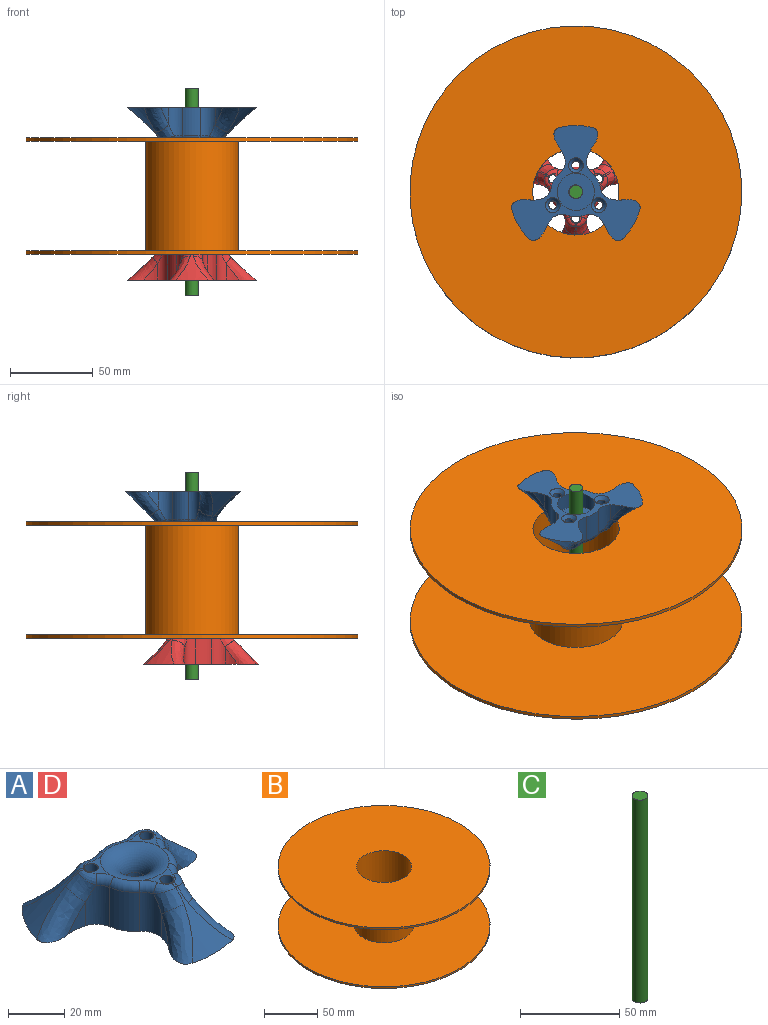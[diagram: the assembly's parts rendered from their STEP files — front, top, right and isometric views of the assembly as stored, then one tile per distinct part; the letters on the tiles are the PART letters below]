
ASSEMBLY  parts=4 mates=3
PART A: 62 faces, bbox 88.5x80.4x33.9 mm
  f0: plane 12.74x8.35mm, normal (0,0,1), area 30.5mm2, adj f13,f44,f46,f48,f50,f52,f61
  f1: plane 11.39x10.93mm, normal (0,0,1), area 30.5mm2, adj f11,f45,f47,f49,f51,f53,f61
  f2: cylinder r=20mm len=10.06mm, axis (0,0,-1), area 41.7mm2, adj f15,f26,f39
  f3: cylinder r=15mm len=17mm, axis (0,0,-1), area 190.3mm2, adj f15,f26,f27,f54
  f4: cylinder r=20mm len=10.06mm, axis (0,0,-1), area 41.7mm2, adj f15,f27,f37
  f5: cylinder r=20mm len=10.06mm, axis (0,0,-1), area 41.7mm2, adj f15,f28,f35
  f6: cylinder r=15mm len=17mm, axis (0,0,-1), area 190.3mm2, adj f15,f28,f29,f55
  f7: cylinder r=20mm len=10.06mm, axis (0,0,-1), area 41.7mm2, adj f15,f29,f33
  f8: cylinder r=20mm len=10.06mm, axis (0,0,-1), area 41.7mm2, adj f15,f30,f31
  f9: cylinder r=15mm len=17mm, axis (0,0,-1), area 190.3mm2, adj f15,f25,f30,f43
  f10: cylinder r=20mm len=10.06mm, axis (0,0,-1), area 41.7mm2, adj f15,f25,f41
  f11: cylinder r=2.5mm len=18mm, axis (0,0,-1), area 282.7mm2, adj f1,f23
  f12: cylinder r=2.5mm len=18mm, axis (0,0,-1), area 282.7mm2, adj f20,f24
  f13: cylinder r=2.5mm len=18mm, axis (0,0,-1), area 282.7mm2, adj f0,f22
  f14: cylinder r=11.2mm len=22.4mm, axis (0,0,-1), area 703.7mm2, adj f15,f21
  f15: plane 82.2x74.09mm, normal (0,0,-1), area 1592.4mm2, adj f2,f3,f4,f5,f6,f7,f8,f9
  f16: cone r=20mm half-angle=45deg, axis (0,0,-1), area 210.3mm2, adj f15,f31,f32,f33,f34,f49
  f17: cone r=20mm half-angle=45deg, axis (0,0,-1), area 210.3mm2, adj f15,f39,f40,f41,f42,f48
  f18: cylinder r=4.2mm len=8.4mm, axis (0,0,-1), area 52.8mm2, adj f21,f61
  f19: cone r=20mm half-angle=45deg, axis (0,0,-1), area 210.3mm2, adj f15,f35,f36,f37,f38,f60
  f20: plane 11.39x10.93mm, normal (0,0,1), area 30.5mm2, adj f12,f56,f57,f58,f59,f60,f61
  f21: plane 22.4x22.4mm, normal (0,0,-1), area 338.7mm2, adj f14,f18
  f22: cone r=4.5mm half-angle=45deg, axis (0,0,-1), area 62.2mm2, adj f13,f15
  f23: cone r=4.5mm half-angle=45deg, axis (0,0,-1), area 62.2mm2, adj f11,f15
  f24: cone r=4.5mm half-angle=45deg, axis (0,0,-1), area 62.2mm2, adj f12,f15
  f25: cylinder r=8mm len=17mm, axis (0,0,-1), area 142.1mm2, adj f9,f10,f15,f42,f44
  f26: cylinder r=8mm len=17mm, axis (0,0,-1), area 142.1mm2, adj f2,f3,f15,f40,f52
  f27: cylinder r=8mm len=17mm, axis (0,0,-1), area 142.1mm2, adj f3,f4,f15,f38,f56
  f28: cylinder r=8mm len=17mm, axis (0,0,-1), area 142.1mm2, adj f5,f6,f15,f36,f57
  f29: cylinder r=8mm len=17mm, axis (0,0,-1), area 142.1mm2, adj f6,f7,f15,f34,f53
  f30: cylinder r=8mm len=17mm, axis (0,0,-1), area 142.1mm2, adj f8,f9,f15,f32,f45
  f31: bspline ~24.84x23.53mm, area 183.7mm2, adj f8,f15,f16,f32
  f32: bspline ~12.71x10.25mm, area 67.7mm2, adj f16,f30,f31,f47
  f33: bspline ~24.84x23.26mm, area 183.7mm2, adj f7,f15,f16,f34
  f34: bspline ~13.09x12.45mm, area 67.7mm2, adj f16,f29,f33,f51
  f35: bspline ~24.84x23.26mm, area 183.7mm2, adj f5,f15,f19,f36
  f36: bspline ~13.09x12.45mm, area 67.7mm2, adj f19,f28,f35,f59
  f37: bspline ~24.84x23.53mm, area 183.7mm2, adj f4,f15,f19,f38
  f38: bspline ~12.71x10.25mm, area 67.7mm2, adj f19,f27,f37,f58
  f39: bspline ~22.82x21.44mm, area 183.7mm2, adj f2,f15,f17,f40
  f40: bspline ~13.09x11.26mm, area 67.7mm2, adj f17,f26,f39,f50
  f41: bspline ~24.84x23.2mm, area 183.7mm2, adj f10,f15,f17,f42
  f42: bspline ~13.09x11.26mm, area 67.7mm2, adj f17,f25,f41,f46
  f43: torus R=12mm, axis (0,0,1), area 48.2mm2, adj f9,f44,f45,f61
  f44: torus R=11mm, axis (0,0,1), area 27.6mm2, adj f0,f25,f43,f46,f61
  f45: torus R=11mm, axis (0,0,1), area 27.6mm2, adj f1,f30,f43,f47,f61
  f46: bspline ~7.24x5.81mm, area 23mm2, adj f0,f42,f44,f48
  f47: bspline ~9.05x4.7mm, area 23mm2, adj f1,f32,f45,f49
  f48: torus R=18.76mm, axis (0,0,1), area 2.4mm2, adj f0,f17,f46,f50
  f49: torus R=18.76mm, axis (0,0,1), area 2.4mm2, adj f1,f16,f47,f51
  f50: bspline ~7.78x6.43mm, area 23mm2, adj f0,f40,f48,f52
  f51: bspline ~7.97x4.64mm, area 23mm2, adj f1,f34,f49,f53
  f52: torus R=11mm, axis (0,0,1), area 27.6mm2, adj f0,f26,f50,f54,f61
  f53: torus R=11mm, axis (0,0,1), area 27.6mm2, adj f1,f29,f51,f55,f61
  f54: torus R=12mm, axis (0,0,1), area 48.2mm2, adj f3,f52,f56,f61
  f55: torus R=12mm, axis (0,0,1), area 48.2mm2, adj f6,f53,f57,f61
  f56: torus R=11mm, axis (0,0,1), area 27.6mm2, adj f20,f27,f54,f58,f61
  f57: torus R=11mm, axis (0,0,1), area 27.6mm2, adj f20,f28,f55,f59,f61
  f58: bspline ~8.78x4.22mm, area 23mm2, adj f20,f38,f56,f60
  f59: bspline ~8.95x4.64mm, area 23mm2, adj f20,f36,f57,f60
  f60: torus R=18.76mm, axis (0,0,1), area 2.4mm2, adj f19,f20,f58,f59
  f61: torus R=12.2mm, axis (0,0,1), area 557.2mm2, adj f0,f1,f18,f20,f43,f44,f45,f52
PART B: 8 faces, bbox 200x200x70 mm
  f0: cylinder r=100mm len=200mm, axis (0,0,-1), area 1256.6mm2, adj f2,f3
  f1: cylinder r=26mm len=70mm, axis (0,0,-1), area 11435.4mm2, adj f3,f6
  f2: plane 200x200mm, normal (0,0,1), area 28952.9mm2, adj f0,f4
  f3: plane 200x200mm, normal (0,0,-1), area 29292.2mm2, adj f0,f1
  f4: cylinder r=28mm len=66mm, axis (0,0,-1), area 11611.3mm2, adj f2,f7
  f5: cylinder r=100mm len=200mm, axis (0,0,-1), area 1256.6mm2, adj f6,f7
  f6: plane 200x200mm, normal (0,0,1), area 29292.2mm2, adj f1,f5
  f7: plane 200x200mm, normal (0,0,-1), area 28952.9mm2, adj f4,f5
PART C: 3 faces, bbox 8x8x125 mm
  f0: cylinder r=4mm len=125mm, axis (0,0,-1), area 3141.6mm2, adj f1,f2
  f1: plane 8x8mm, normal (0,0,1), area 50.3mm2, adj f0
  f2: plane 8x8mm, normal (0,0,-1), area 50.3mm2, adj f0
PART D: same geometry as A
PLACE A rot(axis=(1,0,0),180deg) t=(-284.65,-131.63,88.28)mm
PLACE B t=(-284.65,-131.63,0)mm
PLACE C t=(-284.65,-131.63,-0.04)mm
PLACE D t=(-284.65,-131.63,-15.63)mm
MATE cylindrical C.f0 <-> B.f1  axis (0,0,-1) through (-284.65,-131.63,37.46)mm
MATE cylindrical A.f3 <-> C.f0  axis (0,0,1) through (-284.65,-131.63,78.28)mm
MATE slider C.f0 <-> D.f3  axis (0,0,-1) through (-284.65,-131.63,37.46)mm
